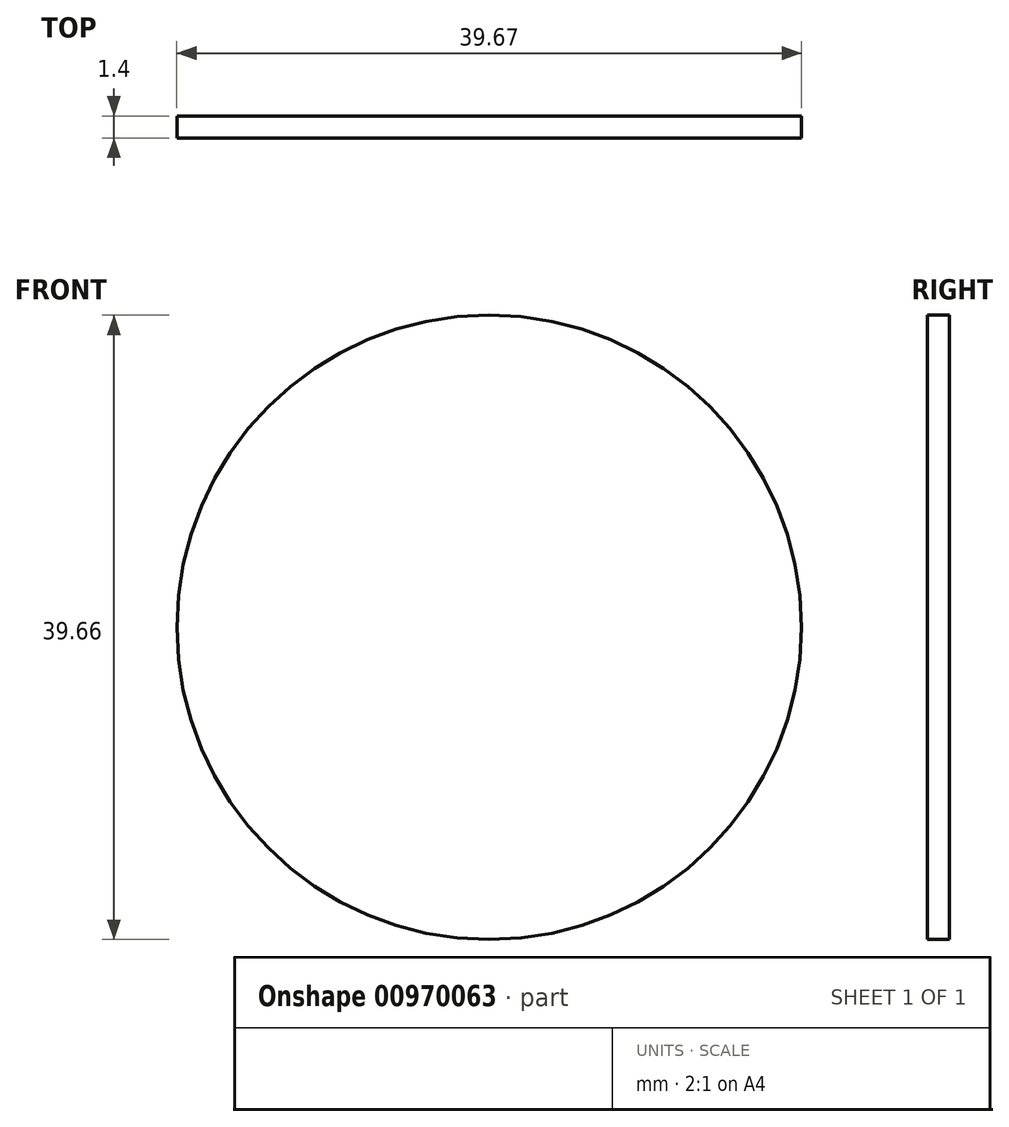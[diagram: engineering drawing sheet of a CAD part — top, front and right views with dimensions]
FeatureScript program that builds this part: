
annotation { "Feature Type Name" : "Feature", "Feature Type Description" : "" }
export const myFeature = defineFeature(function(context is Context, id is Id, definition is map)
    precondition{}
    {
        {
            var Q0;
            Q0=qCreatedBy(makeId("Front.planeOp"),FACE);
            var sketch = newSketch(context, id + "F0", { "sketchPlane" : qUnion([Q0])});
            skCircle(sketch, "E0", {"center": v(2.53, 0) * mm, "radius": 19.83 * mm});
            skSolve(sketch);
        }
        {
            var Q0;
            Q0=makeQuery(id+"F0.imprint","IMPRINT",FACE,{"disambiguationData":[TD([[makeQuery(id+"F0.imprint","IMPRINT",EDGE,{"derivedFrom":sQuery(id+"F0.wireOp",EDGE,"E0")}),1.0]])]});
            var Q1;
            Q1=sQuery(id+"F0.wireOp",EDGE,"E0");
            extrude(context, id + "F1", {"entities" : qUnion([Q0]), "surfaceOperationType" : NewSurfaceOperationType.ADD, "surfaceEntities" : qUnion([Q1]), "depth" : 1.4 * mm, "offsetDistance" : 25 * mm});
        }
    });
